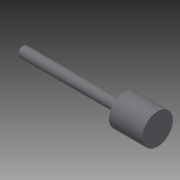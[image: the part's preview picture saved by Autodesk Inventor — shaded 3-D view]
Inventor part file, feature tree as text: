
AUTODESK INVENTOR PART (.ipt)
format: ipt  version: 2014 (Build 180170000, 170)  size: 119,296 bytes
history: native  units: in
note: dims shown in document units (in); Inventor stores cm internally (conversion verified against a paired STEP export)
features: other x49, revolve x2, sketch x2
ambient origin geometry x8: Origin, YZ Plane, XZ Plane, XY Plane, X Axis, Y Axis, Z Axis, Center Point
bodies: Solid1 (feature_tree)
feature tree (53):
  revolve  "Revolution1"  Angle=360.0deg
  revolve  "Revolution2"  [1 undecoded]
  other  "h1_XY"
  other  "h1_YZ"
  other  "h1_ZX"
  other  "h1_X"
  other  "h1_Y"
  other  "h1_Z"
  other  "h1_Center"
  other  "h2_XY"
  other  "h2_YZ"
  other  "h2_ZX"
  other  "h2_X"
  other  "h2_Y"
  other  "h2_Z"
  other  "h2_Center"
  other  "k1_XY"
  other  "k1_YZ"
  other  "k1_ZX"
  other  "k1_X"
  other  "k1_Y"
  other  "k1_Z"
  other  "k1_Center"
  other  "k2_XY"
  other  "k2_YZ"
  other  "k2_ZX"
  other  "k2_X"
  other  "k2_Y"
  other  "k2_Z"
  other  "k2_Center"
  other  "start_XY"
  other  "start_YZ"
  other  "start_ZX"
  other  "start_X"
  other  "start_Y"
  other  "start_Z"
  other  "start_Center"
  other  "to_prc_XY"
  other  "to_prc_YZ"
  other  "to_prc_ZX"
  other  "to_prc_X"
  other  "to_prc_Y"
  other  "to_prc_Z"
  other  "to_prc_Center"
  other  "to_rod_guide_XY"
  other  "to_rod_guide_YZ"
  other  "to_rod_guide_ZX"
  other  "to_rod_guide_X"
  other  "to_rod_guide_Y"
  other  "to_rod_guide_Z"
  other  "to_rod_guide_Center"
  sketch  "Sketch_5"  dims[d0=360.0deg d1=360.0deg]
  sketch  "Sketch_14"
note: 1 required parameter value undecoded (feature->parameter linkage not recoverable at this tier; creation-order binding heuristic only, values carry confidence <= 0.55)
